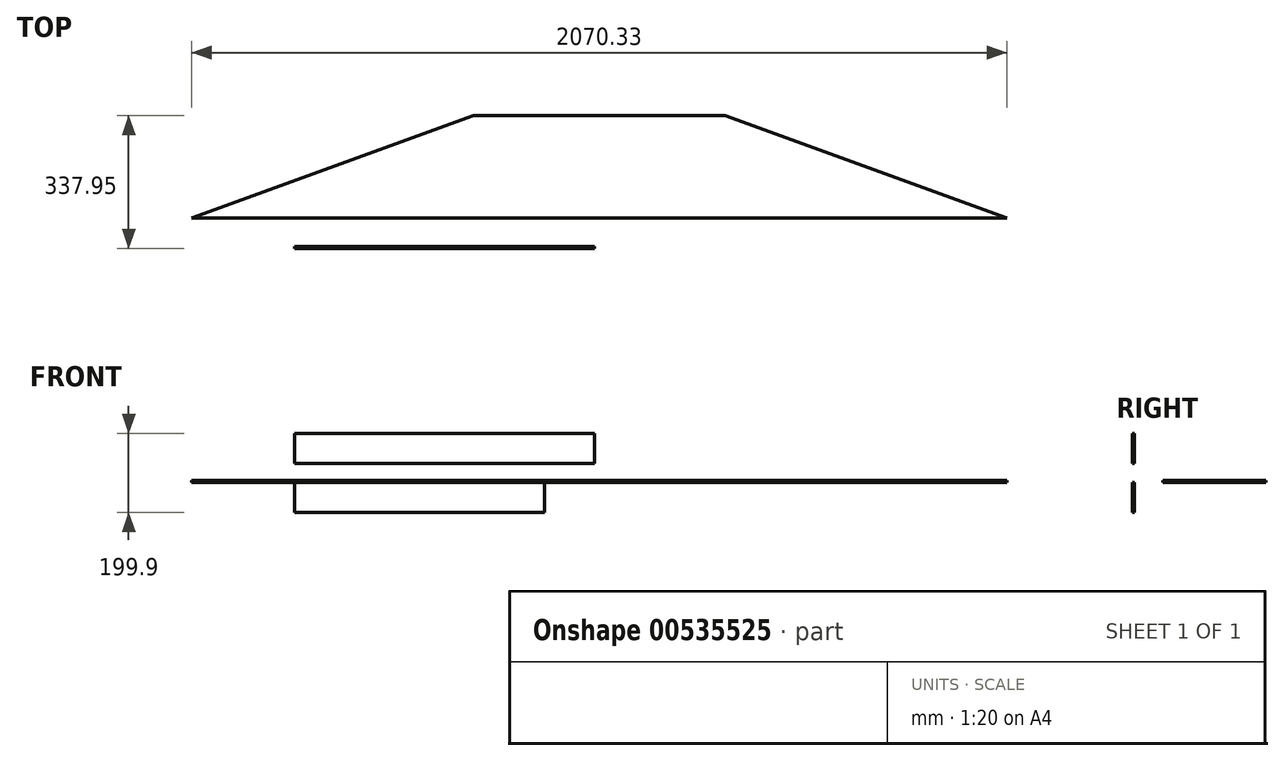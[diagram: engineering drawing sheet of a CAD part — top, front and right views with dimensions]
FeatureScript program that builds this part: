
annotation { "Feature Type Name" : "Feature", "Feature Type Description" : "" }
export const myFeature = defineFeature(function(context is Context, id is Id, definition is map)
    precondition{}
    {
        {
            var Q0;
            Q0=qCreatedBy(makeId("Front.planeOp"),FACE);
            var sketch = newSketch(context, id + "F0", { "sketchPlane" : qUnion([Q0])});
            skLineSegment(sketch, "E0", {"start": v(0, 0) * mm, "end": v(635, 0) * mm});
            skLineSegment(sketch, "E1", {"start": v(635, 0) * mm, "end": v(635, -76.2) * mm});
            skLineSegment(sketch, "E2", {"start": v(635, -76.2) * mm, "end": v(0, -76.2) * mm});
            skLineSegment(sketch, "E3", {"start": v(0, -76.2) * mm, "end": v(0, 0) * mm});
            skSolve(sketch);
        }
        {
            var Q0;
            Q0=makeQuery(id+"F0.imprint","IMPRINT",FACE,{"disambiguationData":[TD([[makeQuery(id+"F0.imprint","IMPRINT",EDGE,{"derivedFrom":sQuery(id+"F0.wireOp",EDGE,"E0")}),-1.0]])]});
            extrude(context, id + "F1", {"entities" : qUnion([Q0]), "depth" : 4.76 * mm, "offsetDistance" : 25.4 * mm});
        }
        {
            var Q0;
            Q0=qCreatedBy(makeId("Front.planeOp"),FACE);
            var sketch = newSketch(context, id + "F2", { "sketchPlane" : qUnion([Q0])});
            skLineSegment(sketch, "E4", {"start": v(0, 47.5) * mm, "end": v(762, 47.5) * mm});
            skLineSegment(sketch, "E5", {"start": v(762, 47.5) * mm, "end": v(762, 123.7) * mm});
            skLineSegment(sketch, "E6", {"start": v(762, 123.7) * mm, "end": v(0, 123.7) * mm});
            skLineSegment(sketch, "E7", {"start": v(0, 123.7) * mm, "end": v(0, 47.5) * mm});
            skSolve(sketch);
        }
        {
            var Q0;
            Q0=makeQuery(id+"F2.imprint","IMPRINT",FACE,{"disambiguationData":[TD([[makeQuery(id+"F2.imprint","IMPRINT",EDGE,{"derivedFrom":sQuery(id+"F2.wireOp",EDGE,"E4")}),1.0]])]});
            extrude(context, id + "F3", {"entities" : qUnion([Q0]), "depth" : 4.76 * mm, "offsetDistance" : 25.4 * mm});
        }
        {
            var Q0;
            Q0=qCreatedBy(makeId("Top.planeOp"),FACE);
            var sketch = newSketch(context, id + "F4", { "sketchPlane" : qUnion([Q0])});
            skLineSegment(sketch, "E8", {"start": v(-260.9, 72.57) * mm, "end": v(1809.43, 72.57) * mm});
            skLineSegment(sketch, "E9", {"start": v(1809.43, 72.57) * mm, "end": v(1093.39, 333.19) * mm});
            skLineSegment(sketch, "E10", {"start": v(-260.9, 72.57) * mm, "end": v(455.15, 333.19) * mm});
            skLineSegment(sketch, "E11", {"start": v(455.15, 333.19) * mm, "end": v(1093.39, 333.19) * mm});
            skSolve(sketch);
        }
        {
            var Q0;
            Q0=makeQuery(id+"F4.imprint","IMPRINT",FACE,{"disambiguationData":[TD([[makeQuery(id+"F4.imprint","IMPRINT",EDGE,{"derivedFrom":sQuery(id+"F4.wireOp",EDGE,"E8")}),1.0]])]});
            extrude(context, id + "F5", {"entities" : qUnion([Q0]), "depth" : 4.76 * mm, "offsetDistance" : 25.4 * mm});
        }
    });
